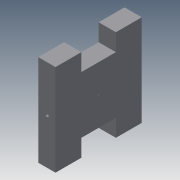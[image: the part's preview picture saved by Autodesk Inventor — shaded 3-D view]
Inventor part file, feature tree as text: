
AUTODESK INVENTOR PART (.ipt)
format: ipt  version: 2013 (Build 170138000, 138)  size: 100,352 bytes
history: native  units: mm
features: sketch x6, hole x2, extrude x1
ambient origin geometry x8: Origin, YZ Plane, XZ Plane, XY Plane, X Axis, Y Axis, Z Axis, Center Point
bodies: Solid1 (feature_tree)
feature tree (9):
  sketch  "Sketch1"  dims[d0=50.0mm d1=53.0mm]
  sketch  "Sketch2"  dims[d2=15.0mm d3=10.0mm]
  extrude  "Extrusion1"  Depth=53.0mm
  sketch  "Sketch4"  dims[d6=15.0mm]
  hole  "Hole1"  [1 undecoded]
  hole  "Hole2"  [1 undecoded]
  sketch  "Sketch3"  dims[d4=20.0mm d5=10.0mm]
  sketch  "Sketch5"  dims[d7=10.0mm]
  sketch  "Sketch6"  dims[d8=20.0mm d9=10.0mm d10=15.0mm d11=10.0mm d12=0.0mm d13=0.4mm d14=0.4mm d15=6.0mm d16=4.0mm d17=2.0mm d18=90.0deg d19=10.0mm d20=0.0mm d21=2.0mm d22=6.0mm d23=4.0mm d24=2.0mm d25=90.0deg d26=50.0mm d27=0.0mm]
note: 2 required parameter values undecoded (feature->parameter linkage not recoverable at this tier; creation-order binding heuristic only, values carry confidence <= 0.55)
